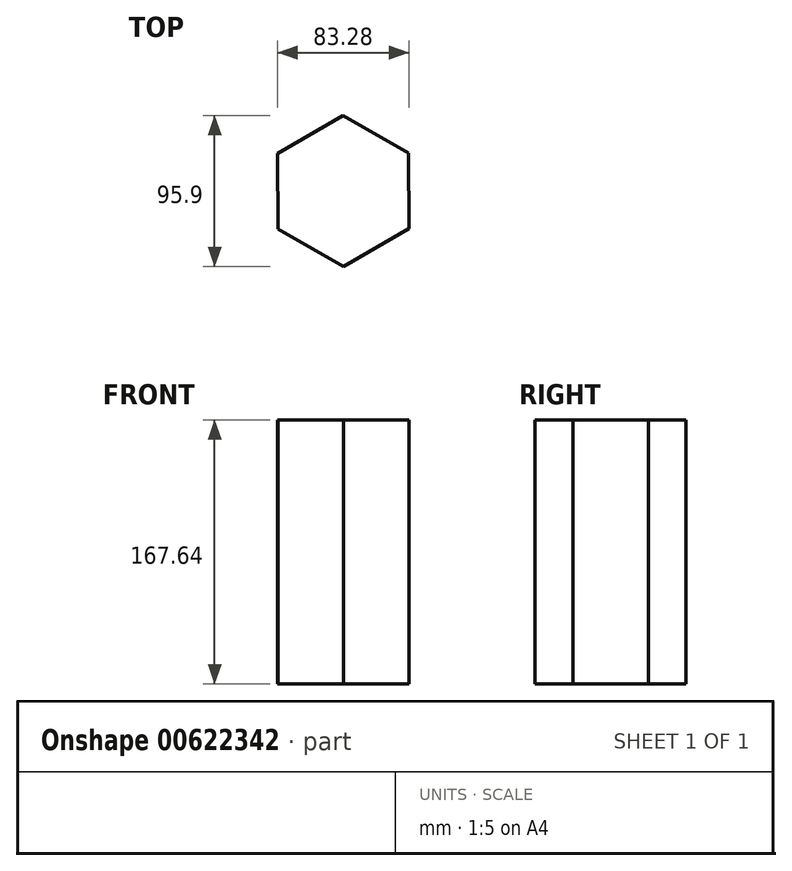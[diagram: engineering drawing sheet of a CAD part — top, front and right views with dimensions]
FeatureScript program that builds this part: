
annotation { "Feature Type Name" : "Feature", "Feature Type Description" : "" }
export const myFeature = defineFeature(function(context is Context, id is Id, definition is map)
    precondition{}
    {
        {
            var Q0;
            Q0=qCreatedBy(makeId("Top.planeOp"),FACE);
            var sketch = newSketch(context, id + "F0", { "sketchPlane" : qUnion([Q0])});
            skCircle(sketch, "E0.cCircle", {"center": v(0, 0) * mm, "radius": 41.53 * mm, "construction": true});
            skLineSegment(sketch, "E0.0", {"start": v(41.64, -23.77) * mm, "end": v(0.23, -47.95) * mm});
            skLineSegment(sketch, "E0.1", {"start": v(0.23, -47.95) * mm, "end": v(-41.4, -24.18) * mm});
            skLineSegment(sketch, "E0.2", {"start": v(-41.4, -24.18) * mm, "end": v(-41.64, 23.77) * mm});
            skLineSegment(sketch, "E0.3", {"start": v(-41.64, 23.77) * mm, "end": v(-0.23, 47.95) * mm});
            skLineSegment(sketch, "E0.4", {"start": v(-0.23, 47.95) * mm, "end": v(41.4, 24.18) * mm});
            skLineSegment(sketch, "E0.5", {"start": v(41.4, 24.18) * mm, "end": v(41.64, -23.77) * mm});
            skPoint(sketch, "E0.0.midPoint", {"position": v(20.94, -35.86) * mm});
            skSolve(sketch);
        }
        {
            var Q0;
            Q0 = qSketchRegion(id + "F0", true);
            extrude(context, id + "F1", {"entities" : qUnion([Q0]), "depth" : 167.64 * mm, "offsetDistance" : 25.4 * mm});
        }
    });
